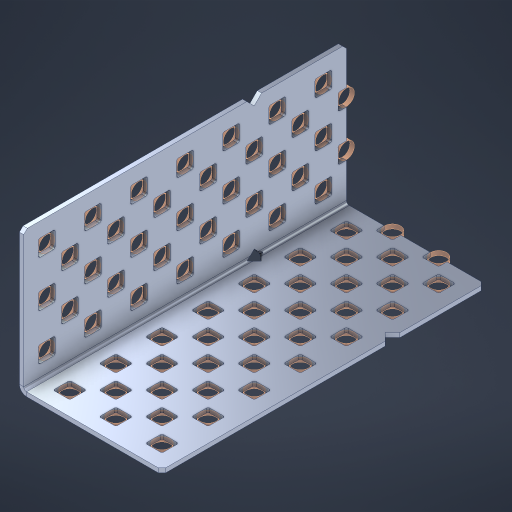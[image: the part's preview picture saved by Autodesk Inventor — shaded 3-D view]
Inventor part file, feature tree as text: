
AUTODESK INVENTOR PART (.ipt)
format: ipt  version: 2023 (Build 270158000, 158)  size: 1,051,136 bytes
history: native  units: in
note: dims shown in document units (in); Inventor stores cm internally (conversion verified against a paired STEP export)
features: other x76, extrude x68, sheet_metal_op x8, sketch x7, pattern_linear x3, mirror x1, chamfer x1
ambient origin geometry x8: Origin, YZ Plane, XZ Plane, XY Plane, X Axis, Y Axis, Z Axis, Center Point
bodies: Solid1 (feature_tree), Body (feature_tree)
feature tree (164):
  sheet_metal_op  "Flanges"
  sheet_metal_op  "Body Pattern"
  pattern_linear  "Center Double"  Spacing1=1.5in  [1 undecoded]
  pattern_linear  "Center Pattern"  Spacing1=0.1875in  [1 undecoded]
  other  "Arc Length"
  pattern_linear  "Notch Pattern"  Spacing1=0.0469in  [1 undecoded]
  other  "Diagonal Plane"
  mirror  "Everything Mirrored"
  chamfer  "End Chamfer"
  sketch  "Sketch1"  dims[d0=1.5in]
  other  "Plate1"
  sketch  "Sketch2"  dims[d1=3.5in]
  other  "Plate2"
  sheet_metal_op  "Bend1"
  sheet_metal_op  "Corner1"
  sketch  "Sketch8"  dims[d2=0.0469in]
  sketch  "Sketch9"  dims[d3=0.0469in]
  other  "Srf91"
  sheet_metal_op  "Body Pattern Sketch"
  other  "Srf92"
  sketch  "Sketch13"  dims[d4=0.0234in]
  sketch  "Sketch15"  dims[d5=0.0938in]
  sketch  "Sketch16"  dims[d6=0.0469in d7=1.5in d8=90.0deg d9=0.0312in d10=0.1875in d11=0.0469in d12=0.0469in d49=0.182in d50=0.02in d52=0.25in d53=0.0469in d54=0.0in d55=0.172in d56=1.0in d57=0.0in d85=0.1473in d86=0.1659in d89=0.0469in d90=0.0in d91=0.04in d92=0.0491in d95=2.5in d96=0.04in d97=0.25in d98=45.0deg d106=0.182in d107=0.02in d110=0.0469in d111=0.0in d112=0.172in d113=0.5in d114=0.0in d117=0.5in d126=0.0491in d127=0.1227in d128=0.08in d129=0.04in d130=2.5in d131=0.25in d132=2.7559in d134=0.5in d135=1.1811in d137=0.5in d140=0.5in d141=1.0in d142=0.3937in d144=0.5in d145=0.071in d146=0.7874in d148=0.5in]
  other  "Srf786"
  other  "Srf856"
  other  "Srf889"
  other  "Srf890"
  other  "Srf891"
  other  "Srf1275"
  other  "Srf1276"
  other  "Srf1278"
  other  "Srf1277"
  other  "Srf1285"
  other  "Srf1286"
  other  "Srf1287"
  other  "Srf1445"
  other  "Srf1446"
  other  "Srf1447"
  other  "Srf1537"
  other  "Srf1538"
  other  "Srf1539"
  other  "Srf2009"
  other  "Srf2010"
  other  "Srf2011"
  other  "Srf2012"
  other  "Srf2013"
  other  "Srf2014"
  other  "Srf2015"
  other  "Srf2043"
  other  "Srf2044"
  other  "Srf2045"
  other  "Srf2046"
  other  "Srf2047"
  other  "Srf2048"
  other  "Srf2076"
  other  "Srf2077"
  other  "Srf2078"
  other  "Srf2079"
  other  "Srf2080"
  other  "Srf2081"
  other  "Srf2082"
  other  "Srf2083"
  other  "Srf2084"
  other  "Srf2085"
  other  "Srf2086"
  other  "Srf2087"
  other  "Srf2088"
  other  "Srf2089"
  other  "Srf2090"
  other  "Srf2091"
  other  "Srf2092"
  other  "Srf2093"
  other  "Srf2094"
  other  "Srf2179"
  other  "Srf2180"
  other  "Srf2181"
  other  "Srf2182"
  other  "Srf2183"
  other  "Srf2184"
  other  "Srf2185"
  other  "Srf2186"
  other  "Srf2187"
  other  "Srf2188"
  other  "Srf2189"
  other  "Srf2190"
  other  "Srf2191"
  other  "Srf2192"
  other  "Srf2193"
  other  "Srf2194"
  other  "Srf2195"
  other  "Srf2196"
  sheet_metal_op  "Body Stamp"
  sheet_metal_op  "Body Circle"
  other  "Center Stamp"
  other  "Center Circle"
  sheet_metal_op  "Notch"
  extrude  "ExtrusionSrf92"  Depth=0.0469in
  extrude  "ExtrusionSrf856"  Depth=0.182in
  extrude  "ExtrusionSrf889"  Depth=0.02in
  extrude  "ExtrusionSrf890"  Depth=0.25in
  extrude  "ExtrusionSrf891"  Depth=0.0469in
  extrude  "ExtrusionSrf1275"  TaperAngle=0.0deg  [1 undecoded]
  extrude  "ExtrusionSrf1276"  Depth=0.5in
  extrude  "ExtrusionSrf1277"  Depth=0.5in TaperAngle=0.0deg
  extrude  "ExtrusionSrf1345"  Depth=0.5in
  extrude  "ExtrusionSrf1346"  Depth=0.5in
  extrude  "ExtrusionSrf1347"  Depth=0.0469in
  extrude  "ExtrusionSrf1348"  Depth=0.5in TaperAngle=0.0deg
  extrude  "ExtrusionSrf1445"  Depth=0.5in
  extrude  "ExtrusionSrf1446"  Depth=0.25in TaperAngle=45.0deg
  extrude  "ExtrusionSrf1447"  Depth=0.182in
  extrude  "ExtrusionSrf1537"  Depth=0.02in
  extrude  "ExtrusionSrf1538"  Depth=0.0469in
  extrude  "ExtrusionSrf1539"  TaperAngle=0.0deg  [1 undecoded]
  extrude  "ExtrusionSrf2009"  Depth=0.5in
  extrude  "ExtrusionSrf2010"  Depth=0.5in TaperAngle=0.0deg
  extrude  "ExtrusionSrf2011"  Depth=0.5in
  extrude  "ExtrusionSrf2012"  Depth=0.5in
  extrude  "ExtrusionSrf2013"  Depth=0.5in
  extrude  "ExtrusionSrf2014"  Depth=0.5in
  extrude  "ExtrusionSrf2015"  Depth=0.5in
  extrude  "ExtrusionSrf2043"  Depth=0.5in
  extrude  "ExtrusionSrf2044"  Depth=0.25in
  extrude  "ExtrusionSrf2045"  Depth=0.5in
  extrude  "ExtrusionSrf2046"  Depth=0.5in
  extrude  "ExtrusionSrf2047"  Depth=0.5in
  extrude  "ExtrusionSrf2048"  Depth=0.5in
  extrude  "ExtrusionSrf2076"  Depth=0.3937in
  extrude  "ExtrusionSrf2077"  Depth=0.5in
  extrude  "ExtrusionSrf2078"  Depth=0.5in
  extrude  "ExtrusionSrf2079"  [1 undecoded]
  extrude  "ExtrusionSrf2080"  [1 undecoded]
  extrude  "ExtrusionSrf2081"  [1 undecoded]
  extrude  "ExtrusionSrf2082"  [1 undecoded]
  extrude  "ExtrusionSrf2083"  [1 undecoded]
  extrude  "ExtrusionSrf2084"  [1 undecoded]
  extrude  "ExtrusionSrf2085"  [1 undecoded]
  extrude  "ExtrusionSrf2086"  [1 undecoded]
  extrude  "ExtrusionSrf2087"  [1 undecoded]
  extrude  "ExtrusionSrf2088"  [1 undecoded]
  extrude  "ExtrusionSrf2089"  [1 undecoded]
  extrude  "ExtrusionSrf2090"  [1 undecoded]
  extrude  "ExtrusionSrf2091"  [1 undecoded]
  extrude  "ExtrusionSrf2092"  [1 undecoded]
  extrude  "ExtrusionSrf2093"  [1 undecoded]
  extrude  "ExtrusionSrf2094"  [1 undecoded]
  extrude  "ExtrusionSrf2179"  [1 undecoded]
  extrude  "ExtrusionSrf2180"  [1 undecoded]
  extrude  "ExtrusionSrf2181"  [1 undecoded]
  extrude  "ExtrusionSrf2182"  [1 undecoded]
  extrude  "ExtrusionSrf2183"  [1 undecoded]
  extrude  "ExtrusionSrf2184"  [1 undecoded]
  extrude  "ExtrusionSrf2185"  [1 undecoded]
  extrude  "ExtrusionSrf2186"  [1 undecoded]
  extrude  "ExtrusionSrf2187"  [1 undecoded]
  extrude  "ExtrusionSrf2188"  [1 undecoded]
  extrude  "ExtrusionSrf2189"  [1 undecoded]
  extrude  "ExtrusionSrf2190"  [1 undecoded]
  extrude  "ExtrusionSrf2191"  [1 undecoded]
  extrude  "ExtrusionSrf2192"  [1 undecoded]
  extrude  "ExtrusionSrf2193"  [1 undecoded]
  extrude  "ExtrusionSrf2194"  [1 undecoded]
  extrude  "ExtrusionSrf2195"  [1 undecoded]
  extrude  "ExtrusionSrf2196"  [1 undecoded]
note: 39 required parameter values undecoded (feature->parameter linkage not recoverable at this tier; creation-order binding heuristic only, values carry confidence <= 0.55)
